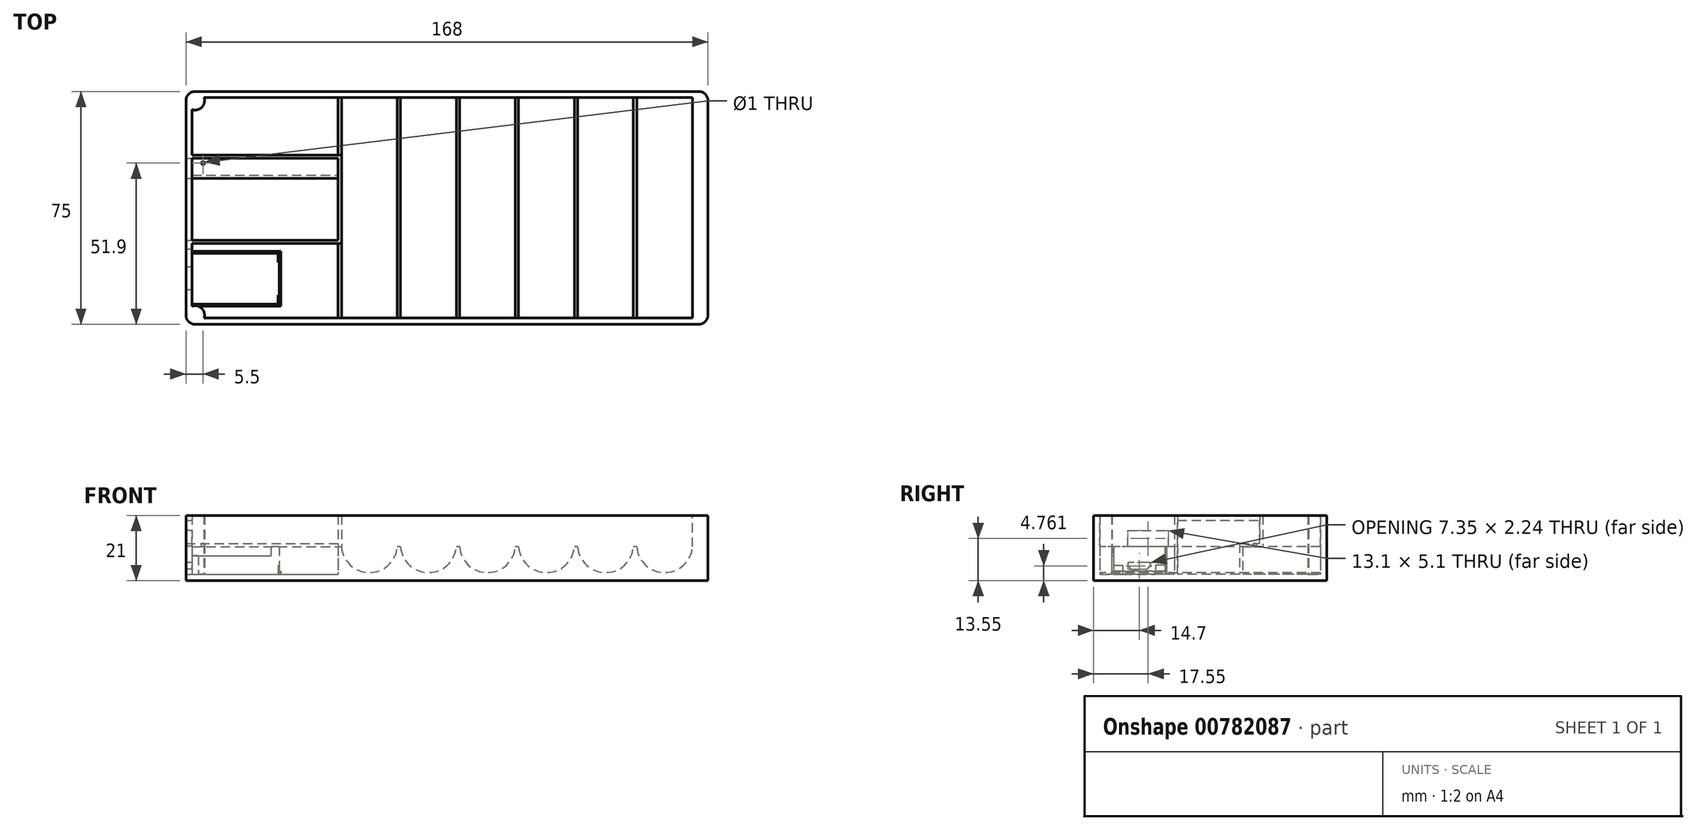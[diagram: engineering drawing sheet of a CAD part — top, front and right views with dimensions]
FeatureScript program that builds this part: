
annotation { "Feature Type Name" : "Feature", "Feature Type Description" : "" }
export const myFeature = defineFeature(function(context is Context, id is Id, definition is map)
    precondition{}
    {
        {
            var Q0;
            Q0=qCreatedBy(makeId("Top.planeOp"),FACE);
            var sketch = newSketch(context, id + "F0", { "sketchPlane" : qUnion([Q0])});
            skLineSegment(sketch, "E0.bottom", {"start": v(-168, 75) * mm, "end": v(0, 75) * mm});
            skLineSegment(sketch, "E0.top", {"start": v(-168, 0) * mm, "end": v(0, 0) * mm});
            skLineSegment(sketch, "E0.left", {"start": v(-168, 75) * mm, "end": v(-168, 0) * mm});
            skLineSegment(sketch, "E0.right", {"start": v(0, 75) * mm, "end": v(0, 0) * mm});
            skSolve(sketch);
        }
        {
            var Q0;
            Q0=makeQuery(id+"F0.imprint","IMPRINT",FACE,{"disambiguationData":[TD([[makeQuery(id+"F0.imprint","IMPRINT",EDGE,{"derivedFrom":sQuery(id+"F0.wireOp",EDGE,"E0.bottom")}),-1.0]])]});
            extrude(context, id + "F1", {"entities" : qUnion([Q0]), "depth" : 21 * mm, "offsetDistance" : 25 * mm});
        }
        {
            var Q0;
            Q0=makeQuery(id+"F1.opExtrude","CAP_FACE",FACE,{"disambiguationData":[OSD([sQuery(id+"F0.wireOp",EDGE,"E0.bottom"),sQuery(id+"F0.wireOp",EDGE,"E0.top"),sQuery(id+"F0.wireOp",EDGE,"E0.left"),sQuery(id+"F0.wireOp",EDGE,"E0.right")])],"isStart":false});
            shell(context, id + "F2", {"entities" : qUnion([Q0]), "thickness" : 2 * mm});
        }
        {
            var Q0;
            Q0=makeQuery(id+"F2.opShell","OFFSET_FACE",FACE,{"disambiguationData":[OSD([sQuery(id+"F0.wireOp",EDGE,"E0.top")])]});
            var sketch = newSketch(context, id + "F3", { "sketchPlane" : qUnion([Q0])});
            skArc(sketch, "E1", {"start": v(5, 10.9) * mm, "mid": v(13.97, 2.6) * mm, "end": v(22.94, 10.9) * mm});
            skLineSegment(sketch, "E2", {"start": v(5, 10.9) * mm, "end": v(22.94, 10.9) * mm});
            skArc(sketch, "E3.1.0.0", {"start": v(24, 10.9) * mm, "mid": v(32.97, 2.6) * mm, "end": v(41.94, 10.9) * mm});
            skLineSegment(sketch, "E3.1.0.1", {"start": v(24, 10.9) * mm, "end": v(41.94, 10.9) * mm});
            skArc(sketch, "E3.2.0.0", {"start": v(43, 10.9) * mm, "mid": v(51.97, 2.6) * mm, "end": v(60.94, 10.9) * mm});
            skLineSegment(sketch, "E3.2.0.1", {"start": v(43, 10.9) * mm, "end": v(60.94, 10.9) * mm});
            skArc(sketch, "E3.3.0.0", {"start": v(62, 10.9) * mm, "mid": v(70.97, 2.6) * mm, "end": v(79.94, 10.9) * mm});
            skLineSegment(sketch, "E3.3.0.1", {"start": v(62, 10.9) * mm, "end": v(79.94, 10.9) * mm});
            skArc(sketch, "E3.4.0.0", {"start": v(81, 10.9) * mm, "mid": v(89.97, 2.6) * mm, "end": v(98.94, 10.9) * mm});
            skLineSegment(sketch, "E3.4.0.1", {"start": v(81, 10.9) * mm, "end": v(98.94, 10.9) * mm});
            skArc(sketch, "E3.5.0.0", {"start": v(100, 10.9) * mm, "mid": v(108.97, 2.6) * mm, "end": v(117.94, 10.9) * mm});
            skLineSegment(sketch, "E3.5.0.1", {"start": v(100, 10.9) * mm, "end": v(117.94, 10.9) * mm});
            skLineSegment(sketch, "E3.direction1", {"start": v(5, 10.9) * mm, "end": v(24, 10.9) * mm, "construction": true});
            skLineSegment(sketch, "E4", {"start": v(22.94, 10.9) * mm, "end": v(24, 10.9) * mm});
            skLineSegment(sketch, "E5", {"start": v(41.94, 10.9) * mm, "end": v(43, 10.9) * mm});
            skLineSegment(sketch, "E6", {"start": v(60.94, 10.9) * mm, "end": v(62, 10.9) * mm});
            skLineSegment(sketch, "E7", {"start": v(79.94, 10.9) * mm, "end": v(81, 10.9) * mm});
            skLineSegment(sketch, "E8", {"start": v(98.94, 10.9) * mm, "end": v(100, 10.9) * mm});
            skLineSegment(sketch, "E9", {"start": v(117.94, 10.9) * mm, "end": v(119, 10.9) * mm});
            skLineSegment(sketch, "E10", {"start": v(119, 10.9) * mm, "end": v(119, 2) * mm});
            skLineSegment(sketch, "E11", {"start": v(5, 10.9) * mm, "end": v(2, 10.9) * mm, "construction": true});
            skLineSegment(sketch, "E12", {"start": v(5, 10.9) * mm, "end": v(5, 21) * mm});
            skLineSegment(sketch, "E13", {"start": v(5, 21) * mm, "end": v(2, 21) * mm});
            skSolve(sketch);
        }
        {
            var Q0;
            Q0=makeQuery(id+"F3.imprint","IMPRINT",FACE,{"disambiguationData":[TD([[makeQuery(id+"F3.imprint","IMPRINT",EDGE,{"derivedFrom":sQuery(id+"F3.wireOp",EDGE,"E1")}),-1.0]])]});
            var Q1;
            Q1=makeQuery(id+"F2.opShell","OFFSET_FACE",FACE,{"disambiguationData":[OSD([sQuery(id+"F0.wireOp",EDGE,"E0.bottom")])]});
            extrude(context, id + "F4", {"entities" : qUnion([Q0]), "operationType" : NewBodyOperationType.ADD, "endBound" : BoundingType.UP_TO_SURFACE, "depth" : 25 * mm, "endBoundEntityFace" : qUnion([Q1]), "offsetDistance" : 25 * mm});
        }
        {
            var Q0;
            Q0=makeQuery(id+"F1.opExtrude","SWEPT_EDGE",EDGE,{"disambiguationData":[OSD([sQuery(id+"F0.wireOp",EDGE,"E0.bottom"),sQuery(id+"F0.wireOp",EDGE,"E0.right")])]});
            var Q1;
            Q1=makeQuery(id+"F1.opExtrude","SWEPT_EDGE",EDGE,{"disambiguationData":[OSD([sQuery(id+"F0.wireOp",EDGE,"E0.top"),sQuery(id+"F0.wireOp",EDGE,"E0.right")])]});
            var Q2;
            Q2=makeQuery(id+"F1.opExtrude","SWEPT_EDGE",EDGE,{"disambiguationData":[OSD([sQuery(id+"F0.wireOp",EDGE,"E0.top"),sQuery(id+"F0.wireOp",EDGE,"E0.left")])]});
            var Q3;
            Q3=makeQuery(id+"F1.opExtrude","SWEPT_EDGE",EDGE,{"disambiguationData":[OSD([sQuery(id+"F0.wireOp",EDGE,"E0.bottom"),sQuery(id+"F0.wireOp",EDGE,"E0.left")])]});
            fillet(context, id + "F5", {"entities" : qUnion([Q0, Q1, Q2, Q3]), "tangentPropagation" : true, "radius" : 3 * mm, "defaultsChanged" : true, "vertexSettings" : [], "allowEdgeOverflow" : false});
        }
        {
            var Q0;
            Q0=makeQuery(id+"F2.opShell","OFFSET_FACE",FACE,{"disambiguationData":[OSD([sQuery(id+"F0.wireOp",EDGE,"E0.bottom"),sQuery(id+"F0.wireOp",EDGE,"E0.top"),sQuery(id+"F0.wireOp",EDGE,"E0.left"),sQuery(id+"F0.wireOp",EDGE,"E0.right")])]});
            var sketch = newSketch(context, id + "F6", { "sketchPlane" : qUnion([Q0])});
            skCircle(sketch, "E14", {"center": v(-165, 72) * mm, "radius": 3 * mm});
            skPoint(sketch, "E14.first.point", {"position": v(-166, 73) * mm});
            skPoint(sketch, "E14.second.point", {"position": v(-158.51, 73) * mm});
            skPoint(sketch, "E14.third.point", {"position": v(-166, 65.72) * mm});
            skLineSegment(sketch, "E15", {"start": v(-166, 37.5) * mm, "end": v(-119, 37.5) * mm, "construction": true});
            skCircle(sketch, "E16.MirrorC", {"center": v(-165, 3) * mm, "radius": 3 * mm});
            skSolve(sketch);
        }
        {
            var Q0;
            Q0 = qSketchRegion(id + "F6", true);
            var Q1;
            Q1=makeQuery(id+"F4.boolean.opBoolean","MERGE",FACE,{"derivedFrom":[makeQuery(id+"F1.opExtrude","CAP_FACE",FACE,{"disambiguationData":[OSD([sQuery(id+"F0.wireOp",EDGE,"E0.bottom"),sQuery(id+"F0.wireOp",EDGE,"E0.top"),sQuery(id+"F0.wireOp",EDGE,"E0.left"),sQuery(id+"F0.wireOp",EDGE,"E0.right")])],"isStart":false}),makeQuery(id+"F4.opExtrude","SWEPT_FACE",FACE,{"disambiguationData":[OSD([sQuery(id+"F3.wireOp",EDGE,"E13")])]})]});
            extrude(context, id + "F7", {"entities" : qUnion([Q0]), "operationType" : NewBodyOperationType.ADD, "endBound" : BoundingType.UP_TO_SURFACE, "depth" : 25 * mm, "endBoundEntityFace" : qUnion([Q1]), "offsetDistance" : 25 * mm});
        }
        {
            var Q0;
            Q0=makeQuery(id+"F1.opExtrude","SWEPT_FACE",FACE,{"disambiguationData":[OSD([sQuery(id+"F0.wireOp",EDGE,"E0.left")])]});
            var sketch = newSketch(context, id + "F8", { "sketchPlane" : qUnion([Q0])});
            skLineSegment(sketch, "E17.bottom", {"start": v(-11, 11) * mm, "end": v(-24.1, 11) * mm});
            skLineSegment(sketch, "E17.top", {"start": v(-11, 16.1) * mm, "end": v(-24.1, 16.1) * mm});
            skLineSegment(sketch, "E17.left", {"start": v(-11, 11) * mm, "end": v(-11, 16.1) * mm});
            skLineSegment(sketch, "E17.right", {"start": v(-24.1, 11) * mm, "end": v(-24.1, 16.1) * mm});
            skLineSegment(sketch, "E18", {"start": v(-12.5, 3.64) * mm, "end": v(-16.9, 3.64) * mm});
            skLineSegment(sketch, "E19", {"start": v(-17.4, 3.86) * mm, "end": v(-18.2, 4.77) * mm});
            skLineSegment(sketch, "E20", {"start": v(-17.71, 5.88) * mm, "end": v(-11.69, 5.88) * mm});
            skLineSegment(sketch, "E21", {"start": v(-11.2, 4.77) * mm, "end": v(-12, 3.86) * mm});
            skPoint(sketch, "E22.visualSharp", {"position": v(-19.2, 5.88) * mm});
            skArc(sketch, "E22.filletArc", {"start": v(-17.71, 5.88) * mm, "mid": v(-18.32, 5.49) * mm, "end": v(-18.2, 4.77) * mm});
            skPoint(sketch, "E23.visualSharp", {"position": v(-10.2, 5.88) * mm});
            skArc(sketch, "E23.filletArc", {"start": v(-11.2, 4.77) * mm, "mid": v(-11.08, 5.49) * mm, "end": v(-11.69, 5.88) * mm});
            skPoint(sketch, "E24.visualSharp", {"position": v(-12.2, 3.64) * mm});
            skArc(sketch, "E24.filletArc", {"start": v(-12.5, 3.64) * mm, "mid": v(-12.23, 3.7) * mm, "end": v(-12, 3.86) * mm});
            skPoint(sketch, "E25.visualSharp", {"position": v(-17.2, 3.64) * mm});
            skArc(sketch, "E25.filletArc", {"start": v(-17.4, 3.86) * mm, "mid": v(-17.17, 3.7) * mm, "end": v(-16.9, 3.64) * mm});
            skLineSegment(sketch, "E26", {"start": v(-18.2, 4.77) * mm, "end": v(-11.2, 4.77) * mm, "construction": true});
            skLineSegment(sketch, "E27", {"start": v(-14.7, 3.64) * mm, "end": v(-14.7, 2.64) * mm, "construction": true});
            skLineSegment(sketch, "E28", {"start": v(-12.2, 3.64) * mm, "end": v(-3, 3.64) * mm, "construction": true});
            skLineSegment(sketch, "E29", {"start": v(-11, 11) * mm, "end": v(-3, 11) * mm, "construction": true});
            skLineSegment(sketch, "E30", {"start": v(-24.1, 11) * mm, "end": v(-24.1, 0) * mm, "construction": true});
            skSolve(sketch);
        }
        {
            var Q0;
            Q0 = qSketchRegion(id + "F8", true);
            var Q1;
            Q1=makeQuery(id+"F2.opShell","OFFSET_FACE",FACE,{"disambiguationData":[OSD([sQuery(id+"F0.wireOp",EDGE,"E0.left")])]});
            extrude(context, id + "F9", {"entities" : qUnion([Q0]), "operationType" : NewBodyOperationType.REMOVE, "endBound" : BoundingType.UP_TO_SURFACE, "oppositeDirection" : true, "depth" : 25 * mm, "endBoundEntityFace" : qUnion([Q1]), "offsetDistance" : 25 * mm});
        }
        {
            var Q0;
            Q0=makeQuery(id+"F2.opShell","OFFSET_FACE",FACE,{"disambiguationData":[OSD([sQuery(id+"F0.wireOp",EDGE,"E0.bottom"),sQuery(id+"F0.wireOp",EDGE,"E0.top"),sQuery(id+"F0.wireOp",EDGE,"E0.left"),sQuery(id+"F0.wireOp",EDGE,"E0.right")])]});
            var sketch = newSketch(context, id + "F10", { "sketchPlane" : qUnion([Q0])});
            skLineSegment(sketch, "E31.bottom", {"start": v(-166, 5.83) * mm, "end": v(-138, 5.83) * mm});
            skLineSegment(sketch, "E31.top", {"start": v(-166, 6.43) * mm, "end": v(-138, 6.43) * mm});
            skLineSegment(sketch, "E31.left", {"start": v(-166, 5.83) * mm, "end": v(-166, 6.43) * mm});
            skLineSegment(sketch, "E31.right", {"start": v(-138, 5.83) * mm, "end": v(-138, 6.43) * mm});
            skLineSegment(sketch, "E32", {"start": v(-152, 6.43) * mm, "end": v(-152, 22.93) * mm, "construction": true});
            skLineSegment(sketch, "E33.bottom", {"start": v(-166, 22.93) * mm, "end": v(-138, 22.93) * mm});
            skLineSegment(sketch, "E33.top", {"start": v(-166, 23.53) * mm, "end": v(-138, 23.53) * mm});
            skLineSegment(sketch, "E33.left", {"start": v(-166, 22.93) * mm, "end": v(-166, 23.53) * mm});
            skLineSegment(sketch, "E33.right", {"start": v(-138, 22.93) * mm, "end": v(-138, 23.53) * mm});
            skLineSegment(sketch, "E34", {"start": v(-138, 6.13) * mm, "end": v(-137.91, 6.19) * mm, "construction": true});
            skSolve(sketch);
        }
        {
            var Q0;
            Q0 = qSketchRegion(id + "F10", true);
            extrude(context, id + "F11", {"entities" : qUnion([Q0]), "operationType" : NewBodyOperationType.ADD, "depth" : 6 * mm, "offsetDistance" : 25 * mm});
        }
        {
            var Q0;
            Q0=makeQuery(id+"F2.opShell","OFFSET_FACE",FACE,{"disambiguationData":[OSD([sQuery(id+"F0.wireOp",EDGE,"E0.bottom"),sQuery(id+"F0.wireOp",EDGE,"E0.top"),sQuery(id+"F0.wireOp",EDGE,"E0.left"),sQuery(id+"F0.wireOp",EDGE,"E0.right")])]});
            var sketch = newSketch(context, id + "F12", { "sketchPlane" : qUnion([Q0])});
            skLineSegment(sketch, "E35.bottom", {"start": v(-166, 27) * mm, "end": v(-119, 27) * mm});
            skLineSegment(sketch, "E35.top", {"start": v(-166, 26) * mm, "end": v(-119, 26) * mm});
            skLineSegment(sketch, "E35.left", {"start": v(-166, 27) * mm, "end": v(-166, 26) * mm});
            skLineSegment(sketch, "E35.right", {"start": v(-119, 27) * mm, "end": v(-119, 26) * mm});
            skLineSegment(sketch, "E36", {"start": v(-126.35, 26) * mm, "end": v(-126.35, 2) * mm, "construction": true});
            skSolve(sketch);
        }
        {
            var Q0;
            Q0 = qSketchRegion(id + "F12", true);
            var Q1;
            Q1=makeQuery(id+"F7.boolean.opBoolean","MERGE",FACE,{"derivedFrom":[makeQuery(id+"F4.boolean.opBoolean","MERGE",FACE,{"derivedFrom":[makeQuery(id+"F1.opExtrude","CAP_FACE",FACE,{"disambiguationData":[OSD([sQuery(id+"F0.wireOp",EDGE,"E0.bottom"),sQuery(id+"F0.wireOp",EDGE,"E0.top"),sQuery(id+"F0.wireOp",EDGE,"E0.left"),sQuery(id+"F0.wireOp",EDGE,"E0.right")])],"isStart":false}),makeQuery(id+"F4.opExtrude","SWEPT_FACE",FACE,{"disambiguationData":[OSD([sQuery(id+"F3.wireOp",EDGE,"E13")])]})]}),makeQuery(id+"F7.opExtrude","CAP_FACE",FACE,{"disambiguationData":[OSD([sQuery(id+"F6.wireOp",EDGE,"E14")])],"isStart":false}),makeQuery(id+"F7.opExtrude","CAP_FACE",FACE,{"disambiguationData":[OSD([sQuery(id+"F6.wireOp",EDGE,"E16.MirrorC")])],"isStart":false})]});
            extrude(context, id + "F13", {"entities" : qUnion([Q0]), "operationType" : NewBodyOperationType.ADD, "endBound" : BoundingType.UP_TO_SURFACE, "depth" : 25 * mm, "endBoundEntityFace" : qUnion([Q1]), "offsetDistance" : 25 * mm});
        }
        {
            var Q0;
            {var subQ0=sQuery(id+"F0.wireOp",EDGE,"E0.left");var subQ1=sQuery(id+"F0.wireOp",EDGE,"E0.bottom");Q0=makeQuery(id+"F13.boolean.opBoolean","SPLIT",FACE,{"disambiguationData":[TD([makeQuery(id+"F2.opShell","OFFSET_FACE",FACE,{"disambiguationData":[OSD([subQ1])]})])],"derivedFrom":makeQuery(id+"F2.opShell","OFFSET_FACE",FACE,{"disambiguationData":[OSD([subQ1,sQuery(id+"F0.wireOp",EDGE,"E0.top"),subQ0,sQuery(id+"F0.wireOp",EDGE,"E0.right")])]})});}
            var sketch = newSketch(context, id + "F14", { "sketchPlane" : qUnion([Q0])});
            skLineSegment(sketch, "E37.bottom", {"start": v(-166, 48) * mm, "end": v(-119, 48) * mm});
            skLineSegment(sketch, "E37.top", {"start": v(-166, 47) * mm, "end": v(-119, 47) * mm});
            skLineSegment(sketch, "E37.left", {"start": v(-166, 48) * mm, "end": v(-166, 47) * mm});
            skLineSegment(sketch, "E37.right", {"start": v(-119, 48) * mm, "end": v(-119, 47) * mm});
            skLineSegment(sketch, "E38", {"start": v(-133, 48) * mm, "end": v(-133, 73) * mm, "construction": true});
            skSolve(sketch);
        }
        {
            var Q0;
            Q0 = qSketchRegion(id + "F14", true);
            var Q1;
            Q1=makeQuery(id+"F4.opExtrude","SWEPT_FACE",FACE,{"disambiguationData":[OSD([sQuery(id+"F3.wireOp",EDGE,"E9")])]});
            extrude(context, id + "F15", {"entities" : qUnion([Q0]), "operationType" : NewBodyOperationType.ADD, "endBound" : BoundingType.UP_TO_SURFACE, "depth" : 8 * mm, "endBoundEntityFace" : qUnion([Q1]), "offsetDistance" : 25 * mm});
        }
        {
            var Q0;
            Q0=makeQuery(id+"F15.boolean.opBoolean","MERGE",FACE,{"derivedFrom":[makeQuery(id+"F4.opExtrude","SWEPT_FACE",FACE,{"disambiguationData":[OSD([sQuery(id+"F3.wireOp",EDGE,"E9")])]}),makeQuery(id+"F15.opExtrude","CAP_FACE",FACE,{"disambiguationData":[OSD([sQuery(id+"F14.wireOp",EDGE,"E37.bottom"),sQuery(id+"F14.wireOp",EDGE,"E37.top"),sQuery(id+"F14.wireOp",EDGE,"E37.left"),sQuery(id+"F14.wireOp",EDGE,"E37.right")])],"isStart":false})]});
            var sketch = newSketch(context, id + "F16", { "sketchPlane" : qUnion([Q0])});
            skLineSegment(sketch, "E39.bottom", {"start": v(-166, 47) * mm, "end": v(-117.94, 47) * mm});
            skLineSegment(sketch, "E39.top", {"start": v(-166, 54.5) * mm, "end": v(-117.94, 54.5) * mm});
            skLineSegment(sketch, "E39.left", {"start": v(-166, 47) * mm, "end": v(-166, 54.5) * mm});
            skLineSegment(sketch, "E39.right", {"start": v(-117.94, 47) * mm, "end": v(-117.94, 54.5) * mm});
            skSolve(sketch);
        }
        {
            var Q0;
            Q0 = qSketchRegion(id + "F16", true);
            extrude(context, id + "F17", {"entities" : qUnion([Q0]), "operationType" : NewBodyOperationType.ADD, "depth" : 1 * mm, "offsetDistance" : 25 * mm});
        }
        {
            var Q0;
            Q0=makeQuery(id+"F17.opExtrude","CAP_FACE",FACE,{"disambiguationData":[OSD([sQuery(id+"F16.wireOp",EDGE,"E39.bottom"),sQuery(id+"F16.wireOp",EDGE,"E39.top"),sQuery(id+"F16.wireOp",EDGE,"E39.left"),sQuery(id+"F16.wireOp",EDGE,"E39.right")])],"isStart":false});
            var sketch = newSketch(context, id + "F18", { "sketchPlane" : qUnion([Q0])});
            skLineSegment(sketch, "E40.bottom", {"start": v(-166, 54.5) * mm, "end": v(-117.94, 54.5) * mm});
            skLineSegment(sketch, "E40.top", {"start": v(-166, 53.5) * mm, "end": v(-117.94, 53.5) * mm});
            skLineSegment(sketch, "E40.left", {"start": v(-166, 54.5) * mm, "end": v(-166, 53.5) * mm});
            skLineSegment(sketch, "E40.right", {"start": v(-117.94, 54.5) * mm, "end": v(-117.94, 53.5) * mm});
            skSolve(sketch);
        }
        {
            var Q0;
            Q0 = qSketchRegion(id + "F18", true);
            var Q1;
            Q1=makeQuery(id+"F13.boolean.opBoolean","MERGE",FACE,{"derivedFrom":[makeQuery(id+"F7.boolean.opBoolean","MERGE",FACE,{"derivedFrom":[makeQuery(id+"F4.boolean.opBoolean","MERGE",FACE,{"derivedFrom":[makeQuery(id+"F1.opExtrude","CAP_FACE",FACE,{"disambiguationData":[OSD([sQuery(id+"F0.wireOp",EDGE,"E0.bottom"),sQuery(id+"F0.wireOp",EDGE,"E0.top"),sQuery(id+"F0.wireOp",EDGE,"E0.left"),sQuery(id+"F0.wireOp",EDGE,"E0.right")])],"isStart":false}),makeQuery(id+"F4.opExtrude","SWEPT_FACE",FACE,{"disambiguationData":[OSD([sQuery(id+"F3.wireOp",EDGE,"E13")])]})]}),makeQuery(id+"F7.opExtrude","CAP_FACE",FACE,{"disambiguationData":[OSD([sQuery(id+"F6.wireOp",EDGE,"E14")])],"isStart":false}),makeQuery(id+"F7.opExtrude","CAP_FACE",FACE,{"disambiguationData":[OSD([sQuery(id+"F6.wireOp",EDGE,"E16.MirrorC")])],"isStart":false})]}),makeQuery(id+"F13.opExtrude","CAP_FACE",FACE,{"disambiguationData":[OSD([sQuery(id+"F12.wireOp",EDGE,"E35.bottom"),sQuery(id+"F12.wireOp",EDGE,"E35.top"),sQuery(id+"F12.wireOp",EDGE,"E35.left"),sQuery(id+"F12.wireOp",EDGE,"E35.right")])],"isStart":false})]});
            extrude(context, id + "F19", {"entities" : qUnion([Q0]), "operationType" : NewBodyOperationType.ADD, "endBound" : BoundingType.UP_TO_SURFACE, "depth" : 25 * mm, "endBoundEntityFace" : qUnion([Q1]), "offsetDistance" : 25 * mm});
        }
        {
            var Q0;
            {var subQ0=sQuery(id+"F14.wireOp",EDGE,"E37.top");Q0=makeQuery(id+"F17.boolean.opBoolean","SPLIT",FACE,{"disambiguationData":[TD([makeQuery(id+"F2.opShell","OFFSET_FACE",FACE,{"disambiguationData":[OSD([sQuery(id+"F0.wireOp",EDGE,"E0.top")])]})])],"derivedFrom":makeQuery(id+"F15.boolean.opBoolean","MERGE",FACE,{"derivedFrom":[makeQuery(id+"F4.opExtrude","SWEPT_FACE",FACE,{"disambiguationData":[OSD([sQuery(id+"F3.wireOp",EDGE,"E9")])]}),makeQuery(id+"F15.opExtrude","CAP_FACE",FACE,{"disambiguationData":[OSD([sQuery(id+"F14.wireOp",EDGE,"E37.bottom"),subQ0,sQuery(id+"F14.wireOp",EDGE,"E37.left"),sQuery(id+"F14.wireOp",EDGE,"E37.right")])],"isStart":false})]})});}
            var sketch = newSketch(context, id + "F20", { "sketchPlane" : qUnion([Q0])});
            skLineSegment(sketch, "E41.bottom", {"start": v(-119, 26) * mm, "end": v(-117.94, 26) * mm});
            skLineSegment(sketch, "E41.top", {"start": v(-119, 47) * mm, "end": v(-117.94, 47) * mm});
            skLineSegment(sketch, "E41.left", {"start": v(-119, 26) * mm, "end": v(-119, 47) * mm});
            skLineSegment(sketch, "E41.right", {"start": v(-117.94, 26) * mm, "end": v(-117.94, 47) * mm});
            skSolve(sketch);
        }
        {
            var Q0;
            Q0 = qSketchRegion(id + "F20", true);
            var Q1;
            Q1=makeQuery(id+"F19.boolean.opBoolean","MERGE",FACE,{"derivedFrom":[makeQuery(id+"F13.boolean.opBoolean","MERGE",FACE,{"derivedFrom":[makeQuery(id+"F7.boolean.opBoolean","MERGE",FACE,{"derivedFrom":[makeQuery(id+"F4.boolean.opBoolean","MERGE",FACE,{"derivedFrom":[makeQuery(id+"F1.opExtrude","CAP_FACE",FACE,{"disambiguationData":[OSD([sQuery(id+"F0.wireOp",EDGE,"E0.bottom"),sQuery(id+"F0.wireOp",EDGE,"E0.top"),sQuery(id+"F0.wireOp",EDGE,"E0.left"),sQuery(id+"F0.wireOp",EDGE,"E0.right")])],"isStart":false}),makeQuery(id+"F4.opExtrude","SWEPT_FACE",FACE,{"disambiguationData":[OSD([sQuery(id+"F3.wireOp",EDGE,"E13")])]})]}),makeQuery(id+"F7.opExtrude","CAP_FACE",FACE,{"disambiguationData":[OSD([sQuery(id+"F6.wireOp",EDGE,"E14")])],"isStart":false}),makeQuery(id+"F7.opExtrude","CAP_FACE",FACE,{"disambiguationData":[OSD([sQuery(id+"F6.wireOp",EDGE,"E16.MirrorC")])],"isStart":false})]}),makeQuery(id+"F13.opExtrude","CAP_FACE",FACE,{"disambiguationData":[OSD([sQuery(id+"F12.wireOp",EDGE,"E35.bottom"),sQuery(id+"F12.wireOp",EDGE,"E35.top"),sQuery(id+"F12.wireOp",EDGE,"E35.left"),sQuery(id+"F12.wireOp",EDGE,"E35.right")])],"isStart":false})]}),makeQuery(id+"F19.opExtrude","CAP_FACE",FACE,{"disambiguationData":[OSD([sQuery(id+"F18.wireOp",EDGE,"E40.bottom"),sQuery(id+"F18.wireOp",EDGE,"E40.top"),sQuery(id+"F18.wireOp",EDGE,"E40.left"),sQuery(id+"F18.wireOp",EDGE,"E40.right")])],"isStart":false})]});
            extrude(context, id + "F21", {"entities" : qUnion([Q0]), "operationType" : NewBodyOperationType.ADD, "endBound" : BoundingType.UP_TO_SURFACE, "depth" : 25 * mm, "endBoundEntityFace" : qUnion([Q1]), "offsetDistance" : 25 * mm});
        }
        {
            var Q0;
            Q0=makeQuery(id+"F17.opExtrude","CAP_FACE",FACE,{"disambiguationData":[OSD([sQuery(id+"F16.wireOp",EDGE,"E39.bottom"),sQuery(id+"F16.wireOp",EDGE,"E39.top"),sQuery(id+"F16.wireOp",EDGE,"E39.left"),sQuery(id+"F16.wireOp",EDGE,"E39.right")])],"isStart":false});
            var sketch = newSketch(context, id + "F22", { "sketchPlane" : qUnion([Q0])});
            skLineSegment(sketch, "E42.bottom", {"start": v(-117.94, 47) * mm, "end": v(-119, 47) * mm});
            skLineSegment(sketch, "E42.top", {"start": v(-117.94, 53.5) * mm, "end": v(-119, 53.5) * mm});
            skLineSegment(sketch, "E42.left", {"start": v(-117.94, 47) * mm, "end": v(-117.94, 53.5) * mm});
            skLineSegment(sketch, "E42.right", {"start": v(-119, 47) * mm, "end": v(-119, 53.5) * mm});
            skSolve(sketch);
        }
        {
            var Q0;
            Q0 = qSketchRegion(id + "F22", true);
            var Q1;
            Q1=makeQuery(id+"F21.boolean.opBoolean","MERGE",FACE,{"derivedFrom":[makeQuery(id+"F19.boolean.opBoolean","MERGE",FACE,{"derivedFrom":[makeQuery(id+"F13.boolean.opBoolean","MERGE",FACE,{"derivedFrom":[makeQuery(id+"F7.boolean.opBoolean","MERGE",FACE,{"derivedFrom":[makeQuery(id+"F4.boolean.opBoolean","MERGE",FACE,{"derivedFrom":[makeQuery(id+"F1.opExtrude","CAP_FACE",FACE,{"disambiguationData":[OSD([sQuery(id+"F0.wireOp",EDGE,"E0.bottom"),sQuery(id+"F0.wireOp",EDGE,"E0.top"),sQuery(id+"F0.wireOp",EDGE,"E0.left"),sQuery(id+"F0.wireOp",EDGE,"E0.right")])],"isStart":false}),makeQuery(id+"F4.opExtrude","SWEPT_FACE",FACE,{"disambiguationData":[OSD([sQuery(id+"F3.wireOp",EDGE,"E13")])]})]}),makeQuery(id+"F7.opExtrude","CAP_FACE",FACE,{"disambiguationData":[OSD([sQuery(id+"F6.wireOp",EDGE,"E14")])],"isStart":false}),makeQuery(id+"F7.opExtrude","CAP_FACE",FACE,{"disambiguationData":[OSD([sQuery(id+"F6.wireOp",EDGE,"E16.MirrorC")])],"isStart":false})]}),makeQuery(id+"F13.opExtrude","CAP_FACE",FACE,{"disambiguationData":[OSD([sQuery(id+"F12.wireOp",EDGE,"E35.bottom"),sQuery(id+"F12.wireOp",EDGE,"E35.top"),sQuery(id+"F12.wireOp",EDGE,"E35.left"),sQuery(id+"F12.wireOp",EDGE,"E35.right")])],"isStart":false})]}),makeQuery(id+"F19.opExtrude","CAP_FACE",FACE,{"disambiguationData":[OSD([sQuery(id+"F18.wireOp",EDGE,"E40.bottom"),sQuery(id+"F18.wireOp",EDGE,"E40.top"),sQuery(id+"F18.wireOp",EDGE,"E40.left"),sQuery(id+"F18.wireOp",EDGE,"E40.right")])],"isStart":false})]}),makeQuery(id+"F21.opExtrude","CAP_FACE",FACE,{"disambiguationData":[OSD([sQuery(id+"F20.wireOp",EDGE,"E41.bottom"),sQuery(id+"F20.wireOp",EDGE,"E41.top"),sQuery(id+"F20.wireOp",EDGE,"E41.left"),sQuery(id+"F20.wireOp",EDGE,"E41.right")])],"isStart":false})]});
            extrude(context, id + "F23", {"entities" : qUnion([Q0]), "operationType" : NewBodyOperationType.ADD, "endBound" : BoundingType.UP_TO_SURFACE, "depth" : 25 * mm, "endBoundEntityFace" : qUnion([Q1]), "offsetDistance" : 25 * mm});
        }
        {
            var Q0;
            {var subQ1=sQuery(id+"F12.wireOp",EDGE,"E35.bottom");var subQ3=makeQuery(id+"F13.opExtrude","SWEPT_FACE",FACE,{"disambiguationData":[OSD([subQ1])]});var subQ5=sQuery(id+"F0.wireOp",EDGE,"E0.left");var subQ12=sQuery(id+"F6.wireOp",EDGE,"E14");Q0=makeQuery(id+"F19.boolean.opBoolean","SPLIT",FACE,{"disambiguationData":[TD([subQ3])],"derivedFrom":makeQuery(id+"F13.boolean.opBoolean","SPLIT",FACE,{"disambiguationData":[TD([makeQuery(id+"F7.opExtrude","SWEPT_FACE",FACE,{"disambiguationData":[OSD([subQ12])]})])],"derivedFrom":makeQuery(id+"F2.opShell","OFFSET_FACE",FACE,{"disambiguationData":[OSD([subQ5])]})})});}
            var sketch = newSketch(context, id + "F24", { "sketchPlane" : qUnion([Q0])});
            skLineSegment(sketch, "E43", {"start": v(35.87, 2) * mm, "end": v(35.87, 2) * mm});
            skLineSegment(sketch, "E44", {"start": v(38.47, 21) * mm, "end": v(38.47, 19.5) * mm, "construction": true});
            skLineSegment(sketch, "E45", {"start": v(27, 11.5) * mm, "end": v(27, 11.5) * mm});
            skLineSegment(sketch, "E46", {"start": v(49.52, 11.9) * mm, "end": v(49.52, 11.9) * mm});
            skLineSegment(sketch, "E47", {"start": v(53.5, 15.57) * mm, "end": v(53.5, 15.57) * mm});
            skLineSegment(sketch, "E48", {"start": v(27, 2) * mm, "end": v(27, 19.5) * mm});
            skLineSegment(sketch, "E49", {"start": v(27, 19.5) * mm, "end": v(53.5, 19.5) * mm});
            skLineSegment(sketch, "E50", {"start": v(53.5, 19.5) * mm, "end": v(53.5, 11.9) * mm});
            skLineSegment(sketch, "E51", {"start": v(53.5, 11.9) * mm, "end": v(47, 11.9) * mm});
            skLineSegment(sketch, "E52", {"start": v(47, 11.9) * mm, "end": v(47, 2) * mm});
            skLineSegment(sketch, "E53", {"start": v(47, 2) * mm, "end": v(27, 2) * mm});
            skLineSegment(sketch, "E54", {"start": v(47, 7.45) * mm, "end": v(47, 7.45) * mm});
            skSolve(sketch);
        }
        {
            var Q0;
            Q0 = qSketchRegion(id + "F24", true);
            var Q1;
            Q1=makeQuery(id+"F1.opExtrude","SWEPT_FACE",FACE,{"disambiguationData":[OSD([sQuery(id+"F0.wireOp",EDGE,"E0.left")])]});
            extrude(context, id + "F25", {"entities" : qUnion([Q0]), "operationType" : NewBodyOperationType.REMOVE, "endBound" : BoundingType.UP_TO_SURFACE, "oppositeDirection" : true, "depth" : 25 * mm, "endBoundEntityFace" : qUnion([Q1]), "offsetDistance" : 25 * mm});
        }
        {
            var Q0;
            Q0=makeQuery(id+"F25.boolean.opBoolean","MERGE",FACE,{"derivedFrom":[makeQuery(id+"F17.opExtrude","CAP_FACE",FACE,{"disambiguationData":[OSD([sQuery(id+"F16.wireOp",EDGE,"E39.bottom"),sQuery(id+"F16.wireOp",EDGE,"E39.top"),sQuery(id+"F16.wireOp",EDGE,"E39.left"),sQuery(id+"F16.wireOp",EDGE,"E39.right")])],"isStart":false})],"fromTools":[makeQuery(id+"F25.opExtrude","SWEPT_FACE",FACE,{"disambiguationData":[OSD([sQuery(id+"F24.wireOp",EDGE,"E51")])]})]});
            var sketch = newSketch(context, id + "F26", { "sketchPlane" : qUnion([Q0])});
            skCircle(sketch, "E55", {"center": v(-162.5, 51.9) * mm, "radius": 0.5 * mm});
            skLineSegment(sketch, "E56", {"start": v(-163, 51.9) * mm, "end": v(-168, 51.9) * mm, "construction": true});
            skSolve(sketch);
        }
        {
            var Q0;
            Q0=makeQuery(id+"F26.imprint","IMPRINT",FACE,{"disambiguationData":[TD([[makeQuery(id+"F26.imprint","IMPRINT",EDGE,{"derivedFrom":sQuery(id+"F26.wireOp",EDGE,"E55")}),1.0]])]});
            extrude(context, id + "F27", {"entities" : qUnion([Q0]), "operationType" : NewBodyOperationType.REMOVE, "endBound" : BoundingType.UP_TO_NEXT, "oppositeDirection" : true, "depth" : 25 * mm, "offsetDistance" : 25 * mm});
        }
        {
            var Q0;
            {var subQ0=sQuery(id+"F0.wireOp",EDGE,"E0.left");var subQ1=sQuery(id+"F0.wireOp",EDGE,"E0.top");Q0=makeQuery(id+"F13.boolean.opBoolean","SPLIT",FACE,{"disambiguationData":[TD([makeQuery(id+"F2.opShell","OFFSET_FACE",FACE,{"disambiguationData":[OSD([subQ1])]})])],"derivedFrom":makeQuery(id+"F2.opShell","OFFSET_FACE",FACE,{"disambiguationData":[OSD([sQuery(id+"F0.wireOp",EDGE,"E0.bottom"),subQ1,subQ0,sQuery(id+"F0.wireOp",EDGE,"E0.right")])]})});}
            var sketch = newSketch(context, id + "F28", { "sketchPlane" : qUnion([Q0])});
            skLineSegment(sketch, "E57.bottom", {"start": v(-138, 6.43) * mm, "end": v(-138.4, 6.43) * mm});
            skLineSegment(sketch, "E57.top", {"start": v(-138, 9.43) * mm, "end": v(-138.4, 9.43) * mm});
            skLineSegment(sketch, "E57.left", {"start": v(-138, 6.43) * mm, "end": v(-138, 9.43) * mm});
            skLineSegment(sketch, "E57.right", {"start": v(-138.4, 6.43) * mm, "end": v(-138.4, 9.43) * mm});
            skLineSegment(sketch, "E58.bottom", {"start": v(-138, 22.93) * mm, "end": v(-138.4, 22.93) * mm});
            skLineSegment(sketch, "E58.top", {"start": v(-138, 19.93) * mm, "end": v(-138.4, 19.93) * mm});
            skLineSegment(sketch, "E58.left", {"start": v(-138, 22.93) * mm, "end": v(-138, 19.93) * mm});
            skLineSegment(sketch, "E58.right", {"start": v(-138.4, 22.93) * mm, "end": v(-138.4, 19.93) * mm});
            skSolve(sketch);
        }
        {
            var Q0;
            Q0 = qSketchRegion(id + "F28", true);
            extrude(context, id + "F29", {"entities" : qUnion([Q0]), "operationType" : NewBodyOperationType.ADD, "depth" : 3 * mm, "offsetDistance" : 25 * mm});
        }
        {
            var Q0;
            {var subQ0=sQuery(id+"F0.wireOp",EDGE,"E0.left");var subQ1=sQuery(id+"F0.wireOp",EDGE,"E0.top");Q0=makeQuery(id+"F13.boolean.opBoolean","SPLIT",FACE,{"disambiguationData":[TD([makeQuery(id+"F2.opShell","OFFSET_FACE",FACE,{"disambiguationData":[OSD([subQ1])]})])],"derivedFrom":makeQuery(id+"F2.opShell","OFFSET_FACE",FACE,{"disambiguationData":[OSD([sQuery(id+"F0.wireOp",EDGE,"E0.bottom"),subQ1,subQ0,sQuery(id+"F0.wireOp",EDGE,"E0.right")])]})});}
            var sketch = newSketch(context, id + "F30", { "sketchPlane" : qUnion([Q0])});
            skLineSegment(sketch, "E59.bottom", {"start": v(-138, 23.53) * mm, "end": v(-137.5, 23.53) * mm});
            skLineSegment(sketch, "E59.top", {"start": v(-138, 5.83) * mm, "end": v(-137.5, 5.83) * mm});
            skLineSegment(sketch, "E59.left", {"start": v(-138, 23.53) * mm, "end": v(-138, 5.83) * mm});
            skLineSegment(sketch, "E59.right", {"start": v(-137.5, 23.53) * mm, "end": v(-137.5, 5.83) * mm});
            skSolve(sketch);
        }
        {
            var Q0;
            Q0 = qSketchRegion(id + "F30", true);
            extrude(context, id + "F31", {"entities" : qUnion([Q0]), "operationType" : NewBodyOperationType.ADD, "depth" : 1 * mm, "offsetDistance" : 25 * mm});
        }
        {
            var Q0;
            Q0=makeQuery(id+"F11.opExtrude","CAP_FACE",FACE,{"disambiguationData":[OSD([sQuery(id+"F10.wireOp",EDGE,"E31.bottom"),sQuery(id+"F10.wireOp",EDGE,"E31.top"),sQuery(id+"F10.wireOp",EDGE,"E31.left"),sQuery(id+"F10.wireOp",EDGE,"E31.right")])],"isStart":false});
            var sketch = newSketch(context, id + "F32", { "sketchPlane" : qUnion([Q0])});
            skLineSegment(sketch, "E60.bottom", {"start": v(-140.6, 5.83) * mm, "end": v(-138, 5.83) * mm});
            skLineSegment(sketch, "E60.top", {"start": v(-140.6, 6.43) * mm, "end": v(-138, 6.43) * mm});
            skLineSegment(sketch, "E60.left", {"start": v(-140.6, 5.83) * mm, "end": v(-140.6, 6.43) * mm});
            skLineSegment(sketch, "E60.right", {"start": v(-138, 5.83) * mm, "end": v(-138, 6.43) * mm});
            skLineSegment(sketch, "E61.bottom", {"start": v(-140.6, 22.93) * mm, "end": v(-138, 22.93) * mm});
            skLineSegment(sketch, "E61.top", {"start": v(-140.6, 23.53) * mm, "end": v(-138, 23.53) * mm});
            skLineSegment(sketch, "E61.left", {"start": v(-140.6, 22.93) * mm, "end": v(-140.6, 23.53) * mm});
            skLineSegment(sketch, "E61.right", {"start": v(-138, 22.93) * mm, "end": v(-138, 23.53) * mm});
            skLineSegment(sketch, "E62", {"start": v(-138, 6.13) * mm, "end": v(-138, 6.13) * mm});
            skSolve(sketch);
        }
        {
            var Q0;
            Q0 = qSketchRegion(id + "F32", true);
            extrude(context, id + "F33", {"entities" : qUnion([Q0]), "operationType" : NewBodyOperationType.ADD, "depth" : 3 * mm, "offsetDistance" : 25 * mm});
        }
    });
